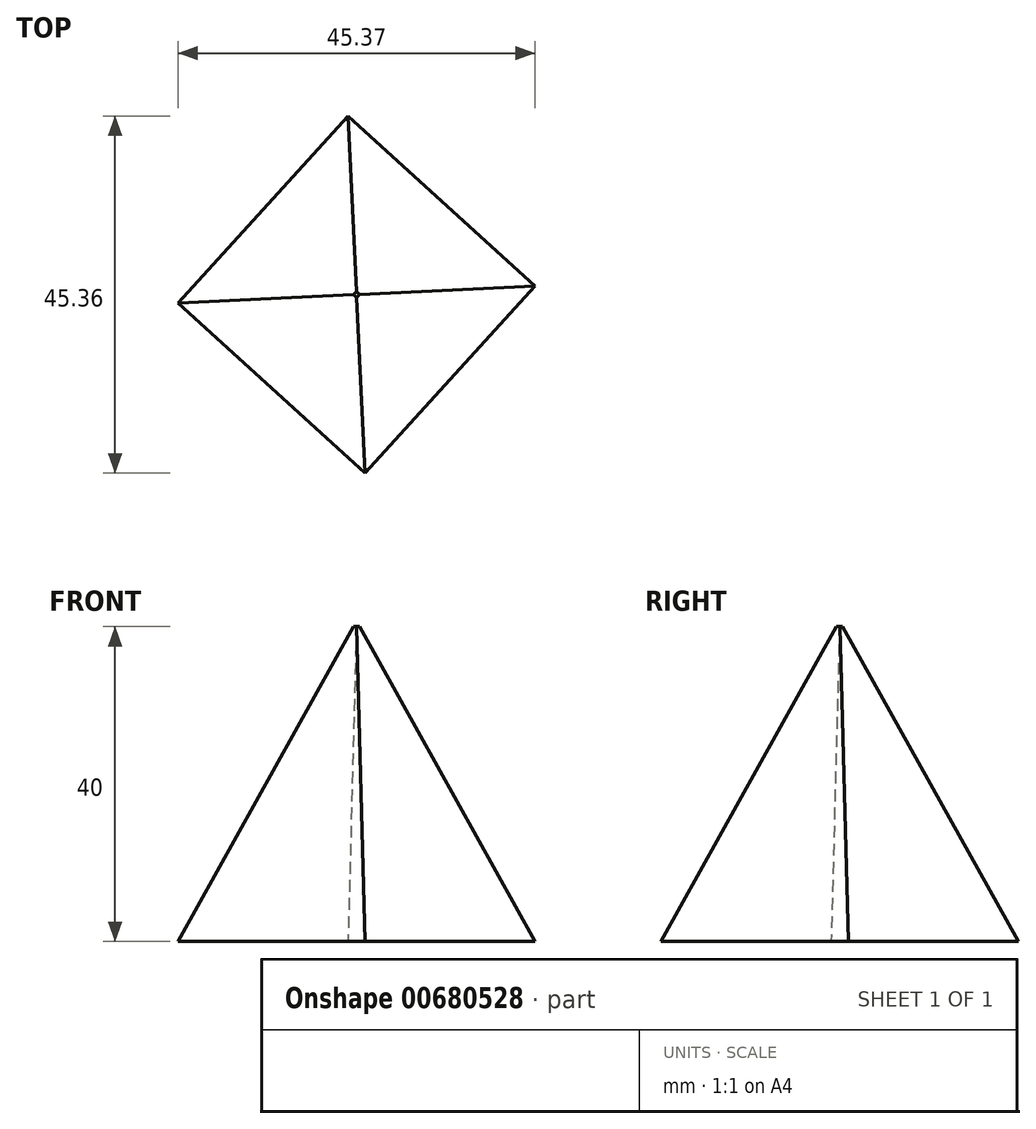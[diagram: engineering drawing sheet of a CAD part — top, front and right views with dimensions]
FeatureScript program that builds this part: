
annotation { "Feature Type Name" : "Feature", "Feature Type Description" : "" }
export const myFeature = defineFeature(function(context is Context, id is Id, definition is map)
    precondition{}
    {
        {
            var Q0;
            Q0=qCreatedBy(makeId("Top.planeOp"),FACE);
            var sketch = newSketch(context, id + "F0", { "sketchPlane" : qUnion([Q0])});
            skCircle(sketch, "E0.cCircle", {"center": v(2, 0) * mm, "radius": 19.32 * mm, "construction": true});
            skLineSegment(sketch, "E0.0", {"start": v(-25.3, -1.3) * mm, "end": v(0.69, 27.29) * mm});
            skLineSegment(sketch, "E0.1", {"start": v(0.69, 27.29) * mm, "end": v(29.28, 1.3) * mm});
            skLineSegment(sketch, "E0.2", {"start": v(29.28, 1.3) * mm, "end": v(3.3, -27.29) * mm});
            skLineSegment(sketch, "E0.3", {"start": v(3.3, -27.29) * mm, "end": v(-25.3, -1.3) * mm});
            skPoint(sketch, "E0.0.midPoint", {"position": v(-12.3, 13) * mm});
            skSolve(sketch);
        }
        {
            var Q0;
            Q0 = qSketchRegion(id + "F0", true);
            extrude(context, id + "F1", {"entities" : qUnion([Q0]), "depth" : 40 * mm, "offsetDistance" : 25.4 * mm});
        }
        {
            var Q0;
            Q0=makeQuery(id+"F1.opExtrude","CAP_EDGE",EDGE,{"disambiguationData":[OSD([sQuery(id+"F0.wireOp",EDGE,"E0.3")])],"isStart":false});
            var Q1;
            Q1=makeQuery(id+"F1.opExtrude","CAP_EDGE",EDGE,{"disambiguationData":[OSD([sQuery(id+"F0.wireOp",EDGE,"E0.0")])],"isStart":false});
            var Q2;
            Q2=makeQuery(id+"F1.opExtrude","CAP_EDGE",EDGE,{"disambiguationData":[OSD([sQuery(id+"F0.wireOp",EDGE,"E0.1")])],"isStart":false});
            var Q3;
            Q3=makeQuery(id+"F1.opExtrude","CAP_EDGE",EDGE,{"disambiguationData":[OSD([sQuery(id+"F0.wireOp",EDGE,"E0.2")])],"isStart":false});
            chamfer(context, id + "F2", {"entities" : qUnion([Q0, Q1, Q2, Q3]), "chamferType" : ChamferType.TWO_OFFSETS, "width1" : 48.26 * mm, "oppositeDirection" : false, "width2" : 19.05 * mm, "tangentPropagation" : true});
        }
    });
